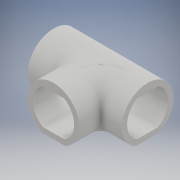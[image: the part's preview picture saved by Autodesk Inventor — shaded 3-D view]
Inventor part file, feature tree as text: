
AUTODESK INVENTOR PART (.ipt)
format: ipt  version: 2017 (Build 210142000, 142)  size: 461,824 bytes
history: native  units: in
note: dims shown in document units (in); Inventor stores cm internally (conversion verified against a paired STEP export)
features: extrude x11, sketch x8, plane x2, sweep x2, mirror x2, other x1, fillet x1
ambient origin geometry x8: Origin, YZ Plane, XZ Plane, XY Plane, X Axis, Y Axis, Z Axis, Center Point
bodies: Solid1 (feature_tree), Solid2 (feature_tree), Solid3 (feature_tree), Solid4 (feature_tree), Solid5 (feature_tree), Solid6 (feature_tree)
feature tree (27):
  sketch  "Sketch1"  dims[d0=6.6667in d1=4.0in d2=9.7746in d3=4.0in d4=0.0in d5=-4.8873in]
  extrude  "corridor"  [1 undecoded]
  extrude  "light right of T"  Depth=4.0in TaperAngle=0.0deg
  plane  "Work Plane1"
  sketch  "Sketch4"  dims[d6=6.6667in d7=4.0in d8=9.7746in d10=4.0in d11=0.0in]
  extrude  "T bottom"  TaperAngle=0.0deg  [1 undecoded]
  extrude  "light bottom of T"  TaperAngle=0.0deg  [1 undecoded]
  sketch  "Sketch8"  dims[d22=9.7746in d23=0.0in]
  sketch  "Sketch7"  dims[d19=4.8873in d20=0.0in d21=0.0in]
  sweep  "corner curve"
  sweep  "light curve right"
  extrude  "flat of T"  Depth=0.0625in
  extrude  "light flat of T"  Depth=0.0892in
  sketch  "Sketch10"  dims[d25=4.0in d26=9.7746in d31=1.0in d32=0.0in]
  mirror  "mirror plane"
  extrude  "other end of T"  Depth=0.0625in TaperAngle=0.0deg
  extrude  "other end of T light"  Depth=0.0625in TaperAngle=0.0deg
  mirror  "corner curve mirror"
  other  "light curve left"
  plane  "Work Plane3"
  extrude  "top hole fill"  TaperAngle=0.0deg  [1 undecoded]
  extrude  "Extrusion18"  Depth=0.0625in TaperAngle=0.0deg
  fillet  "Fillet1"  Radius=4.0in
  extrude  "bottom hole fill"  Depth=0.0625in TaperAngle=0.0deg
  sketch  "Sketch12"  dims[d41=1.0in d42=1.0in]
  sketch  "Sketch15"  dims[d56=0.5833in d57=0.0625in d58=0.0625in d59=0.125in]
  sketch  "Sketch16"  dims[d65=0.25in d66=0.125in d67=45.0deg d68=0.0892in d69=0.0884in d88=0.5833in d89=0.0625in d90=0.0625in d91=0.125in d92=0.25in d93=0.125in d95=0.0892in d96=0.0884in d97=1.0in d98=0.0in d99=1.0in d100=0.0in d101=0.0in d102=0.0in d103=1.0in d104=0.0in d105=4.0in d106=0.0in d107=4.0in d108=0.0in d109=90.0deg d110=3.3333in d112=1.429in d115=4.0in d116=0.0in d117=10.3167in d118=10.3167in d119=0.0417in d120=0.125in d121=0.0in d122=0.0625in]
note: 4 required parameter values undecoded (feature->parameter linkage not recoverable at this tier; creation-order binding heuristic only, values carry confidence <= 0.55)
